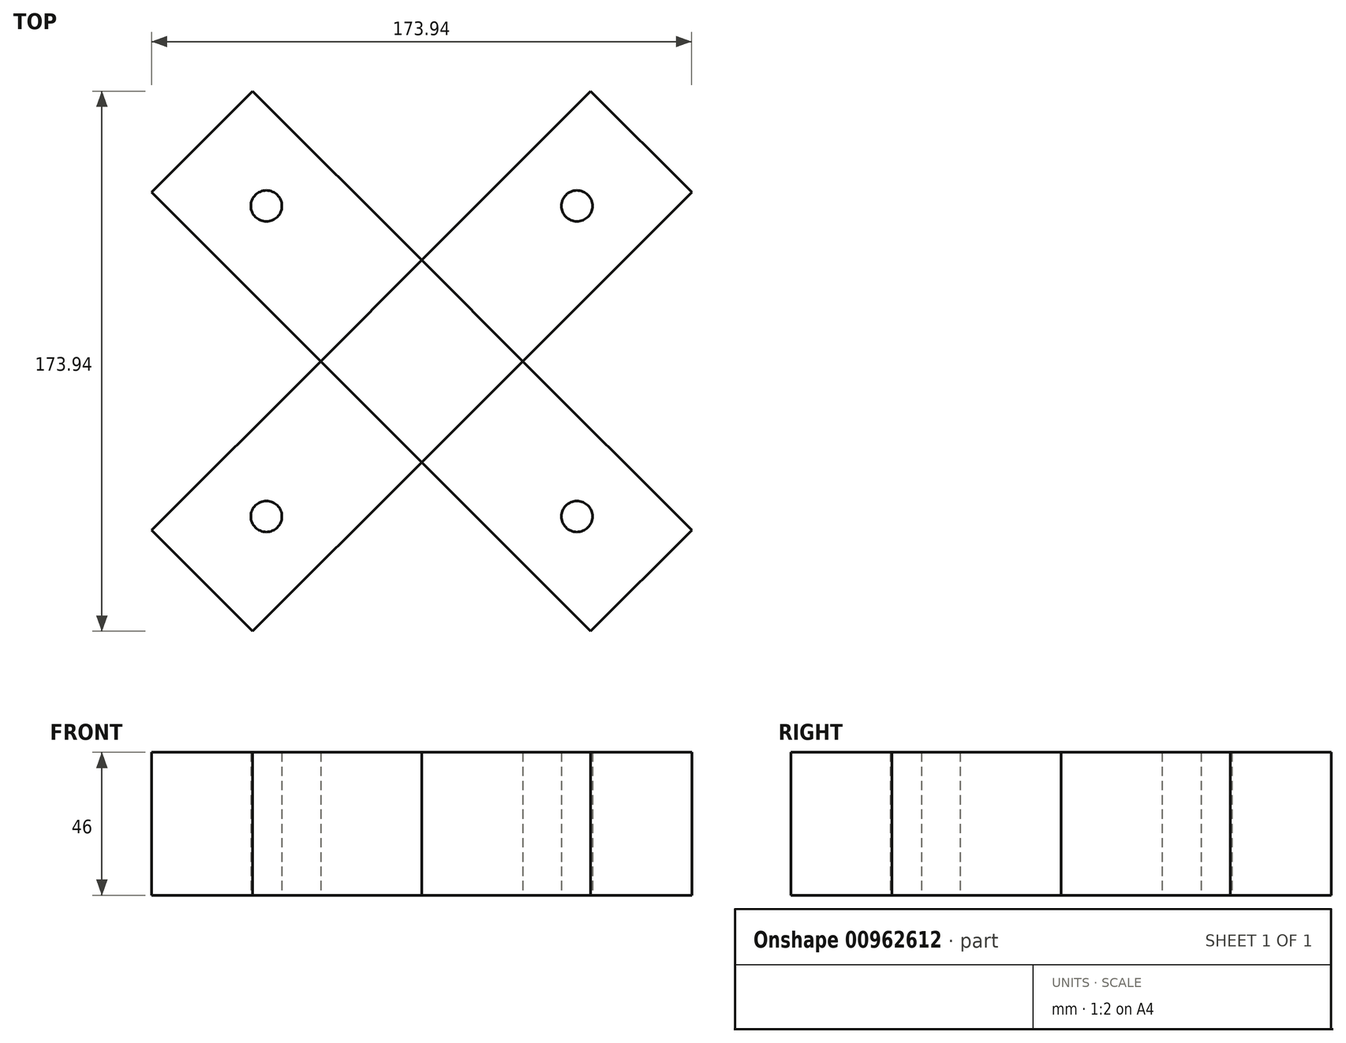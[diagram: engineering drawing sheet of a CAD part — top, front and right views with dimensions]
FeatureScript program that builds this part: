
annotation { "Feature Type Name" : "Feature", "Feature Type Description" : "" }
export const myFeature = defineFeature(function(context is Context, id is Id, definition is map)
    precondition{}
    {
        {
            var Q0;
            Q0=qCreatedBy(makeId("Top.planeOp"),FACE);
            var sketch = newSketch(context, id + "F0", { "sketchPlane" : qUnion([Q0])});
            skLineSegment(sketch, "E0", {"start": v(0, 0) * mm, "end": v(75.34, 75.34) * mm, "construction": true});
            skCircle(sketch, "E1", {"center": v(0, 0) * mm, "radius": 23 * mm, "construction": true});
            skCircle(sketch, "E2", {"center": v(0, 0) * mm, "radius": 100 * mm, "construction": true});
            skLineSegment(sketch, "E3", {"start": v(70.71, 70.71) * mm, "end": v(86.97, 54.45) * mm});
            skLineSegment(sketch, "E4", {"start": v(16.26, 16.26) * mm, "end": v(32.53, 0) * mm});
            skLineSegment(sketch, "E5", {"start": v(32.53, 0) * mm, "end": v(86.97, 54.45) * mm});
            skLineSegment(sketch, "E6.MirrorCS", {"start": v(16.26, 16.26) * mm, "end": v(0, 32.53) * mm});
            skLineSegment(sketch, "E7.MirrorCS", {"start": v(70.71, 70.71) * mm, "end": v(54.45, 86.97) * mm});
            skLineSegment(sketch, "E8.MirrorCS", {"start": v(0, 32.53) * mm, "end": v(54.45, 86.97) * mm});
            skLineSegment(sketch, "E9", {"start": v(0, 0) * mm, "end": v(50, 0) * mm, "construction": true});
            skLineSegment(sketch, "E10", {"start": v(50, 0) * mm, "end": v(50, 50) * mm, "construction": true});
            skCircle(sketch, "E11", {"center": v(50, 50) * mm, "radius": 5 * mm});
            skLineSegment(sketch, "E12", {"start": v(0, 0) * mm, "end": v(24.75, -24.75) * mm, "construction": true});
            skCircle(sketch, "E13.MirrorC", {"center": v(-50, -50) * mm, "radius": 5 * mm});
            skLineSegment(sketch, "E14.MirrorCS", {"start": v(-16.26, -16.26) * mm, "end": v(0, -32.53) * mm});
            skLineSegment(sketch, "E15.MirrorCS", {"start": v(0, -32.53) * mm, "end": v(-54.45, -86.97) * mm});
            skLineSegment(sketch, "E16.MirrorCS", {"start": v(-70.71, -70.71) * mm, "end": v(-54.45, -86.97) * mm});
            skLineSegment(sketch, "E17.MirrorCS", {"start": v(-70.71, -70.71) * mm, "end": v(-86.97, -54.45) * mm});
            skLineSegment(sketch, "E18.MirrorCS", {"start": v(-16.26, -16.26) * mm, "end": v(-32.53, 0) * mm});
            skLineSegment(sketch, "E19.MirrorCS", {"start": v(-32.53, 0) * mm, "end": v(-86.97, -54.45) * mm});
            skSolve(sketch);
        }
        {
            var Q0;
            Q0 = qSketchRegion(id + "F0", true);
            extrude(context, id + "F1", {"entities" : qUnion([Q0]), "depth" : 46 * mm, "offsetDistance" : 25 * mm});
        }
        {
            var Q0;
            Q0=makeQuery(id+"F1.opExtrude","SWEPT_BODY",BODY,{"disambiguationData":[OSD([sQuery(id+"F0.wireOp",EDGE,"E3"),sQuery(id+"F0.wireOp",EDGE,"E4"),sQuery(id+"F0.wireOp",EDGE,"E5"),sQuery(id+"F0.wireOp",EDGE,"E6.MirrorCS"),sQuery(id+"F0.wireOp",EDGE,"E7.MirrorCS"),sQuery(id+"F0.wireOp",EDGE,"E8.MirrorCS"),sQuery(id+"F0.wireOp",EDGE,"E11")])]});
            var Q1;
            Q1=makeQuery(id+"F1.opExtrude","SWEPT_BODY",BODY,{"disambiguationData":[OSD([sQuery(id+"F0.wireOp",EDGE,"E13.MirrorC"),sQuery(id+"F0.wireOp",EDGE,"E14.MirrorCS"),sQuery(id+"F0.wireOp",EDGE,"E15.MirrorCS"),sQuery(id+"F0.wireOp",EDGE,"E16.MirrorCS"),sQuery(id+"F0.wireOp",EDGE,"E17.MirrorCS"),sQuery(id+"F0.wireOp",EDGE,"E18.MirrorCS"),sQuery(id+"F0.wireOp",EDGE,"E19.MirrorCS")])]});
            var Q2;
            Q2=qCreatedBy(makeId("Right.planeOp"),FACE);
            mirror(context, id + "F2", {"entities" : qUnion([Q0, Q1]), "mirrorPlane" : qUnion([Q2])});
        }
    });
